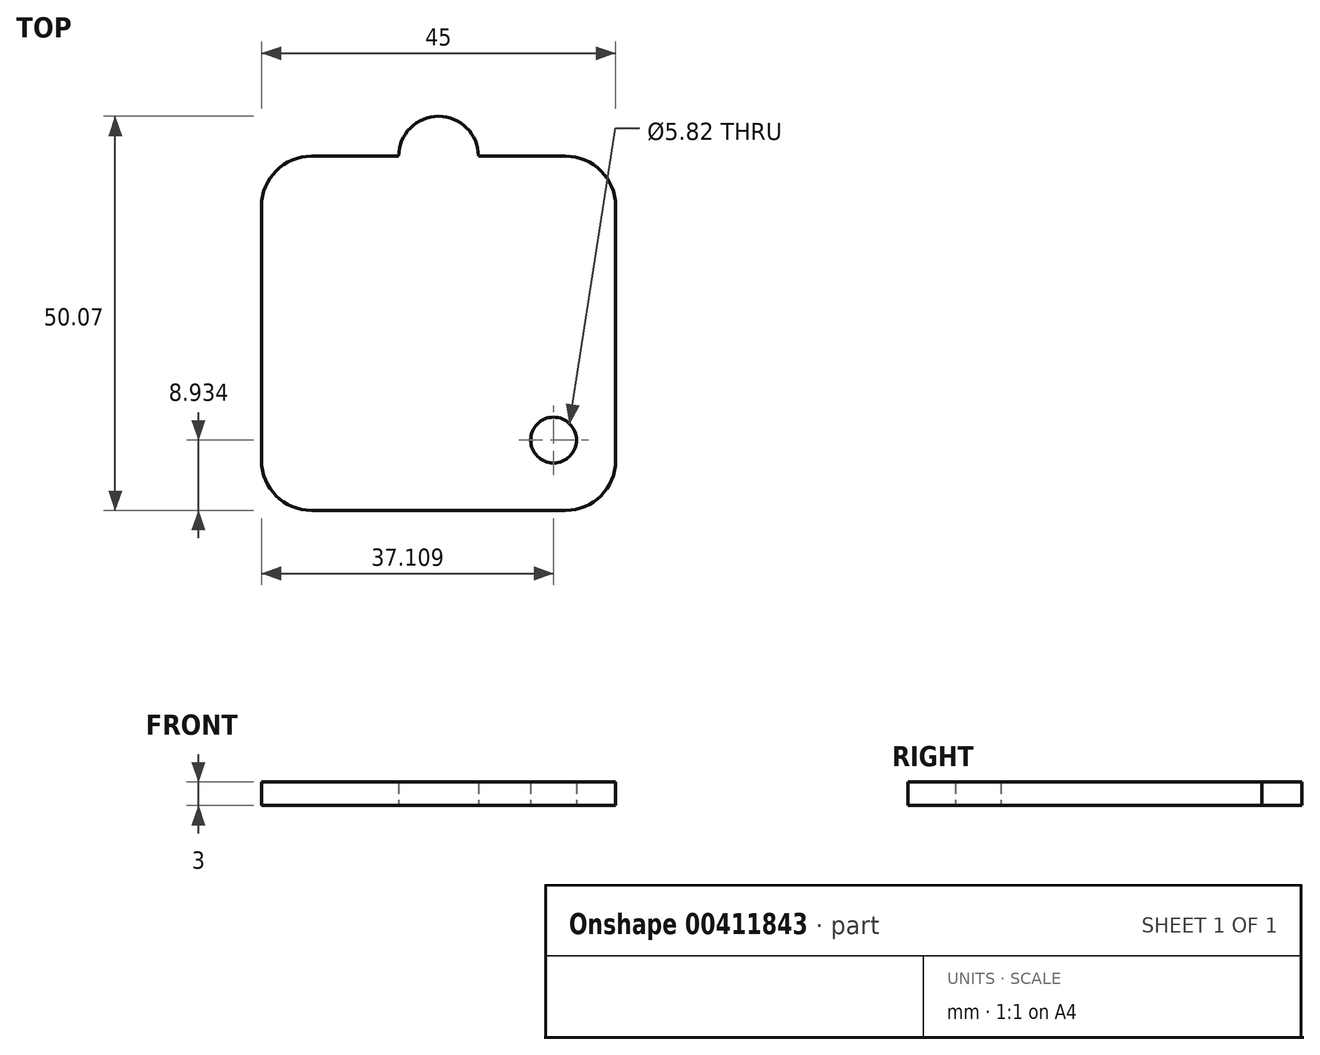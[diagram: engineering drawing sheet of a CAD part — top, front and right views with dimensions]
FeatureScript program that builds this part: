
annotation { "Feature Type Name" : "Feature", "Feature Type Description" : "" }
export const myFeature = defineFeature(function(context is Context, id is Id, definition is map)
    precondition{}
    {
        {
            var Q0;
            Q0=qCreatedBy(makeId("Top.planeOp"),FACE);
            var sketch = newSketch(context, id + "F0", { "sketchPlane" : qUnion([Q0])});
            skLineSegment(sketch, "E0.bottom", {"start": v(16.15, 22.5) * mm, "end": v(-16.15, 22.5) * mm});
            skLineSegment(sketch, "E0.top", {"start": v(16.15, -22.5) * mm, "end": v(-16.15, -22.5) * mm});
            skLineSegment(sketch, "E0.left", {"start": v(22.5, 16.15) * mm, "end": v(22.5, -16.15) * mm});
            skLineSegment(sketch, "E0.right", {"start": v(-22.5, 16.15) * mm, "end": v(-22.5, -16.15) * mm});
            skPoint(sketch, "E0.middle", {"position": v(0, 0) * mm});
            skCircle(sketch, "E1", {"center": v(0, 22.5) * mm, "radius": 5.07 * mm});
            skPoint(sketch, "E2.visualSharp", {"position": v(-22.5, 22.5) * mm});
            skArc(sketch, "E2.filletArc", {"start": v(-16.15, 22.5) * mm, "mid": v(-20.64, 20.64) * mm, "end": v(-22.5, 16.15) * mm});
            skPoint(sketch, "E3.visualSharp", {"position": v(22.5, 22.5) * mm});
            skArc(sketch, "E3.filletArc", {"start": v(22.5, 16.15) * mm, "mid": v(20.64, 20.64) * mm, "end": v(16.15, 22.5) * mm});
            skPoint(sketch, "E4.visualSharp", {"position": v(-22.5, -22.5) * mm});
            skArc(sketch, "E4.filletArc", {"start": v(-22.5, -16.15) * mm, "mid": v(-20.64, -20.64) * mm, "end": v(-16.15, -22.5) * mm});
            skPoint(sketch, "E5.visualSharp", {"position": v(22.5, -22.5) * mm});
            skArc(sketch, "E5.filletArc", {"start": v(16.15, -22.5) * mm, "mid": v(20.64, -20.64) * mm, "end": v(22.5, -16.15) * mm});
            skLineSegment(sketch, "E6.bottom", {"start": v(10, 14.5) * mm, "end": v(-10, 14.5) * mm});
            skLineSegment(sketch, "E6.top", {"start": v(10, -14.5) * mm, "end": v(-10, -14.5) * mm});
            skLineSegment(sketch, "E6.left", {"start": v(10, 14.5) * mm, "end": v(10, -14.5) * mm});
            skLineSegment(sketch, "E6.right", {"start": v(-10, 14.5) * mm, "end": v(-10, -14.5) * mm});
            skPoint(sketch, "E7", {"position": v(-10, 8.5) * mm});
            skPoint(sketch, "E8", {"position": v(-8, 14.5) * mm});
            skCircle(sketch, "E9", {"center": v(-8, 8.5) * mm, "radius": 0.75 * mm});
            skPoint(sketch, "E10", {"position": v(8, -14.5) * mm});
            skPoint(sketch, "E11", {"position": v(10, -8.5) * mm});
            skCircle(sketch, "E12", {"center": v(8, -8.5) * mm, "radius": 0.75 * mm});
            skCircle(sketch, "E13", {"center": v(14.6, -13.57) * mm, "radius": 2.9 * mm});
            skSolve(sketch);
        }
        {
            var Q0;
            Q0=makeQuery(id+"F0.imprint","IMPRINT",FACE,{"disambiguationData":[TD([[makeQuery(id+"F0.imprint","IMPRINT",EDGE,{"derivedFrom":sQuery(id+"F0.wireOp",EDGE,"E9")}),1.0]])]});
            var Q1;
            Q1=makeQuery(id+"F0.imprint","IMPRINT",FACE,{"disambiguationData":[TD([[makeQuery(id+"F0.imprint","IMPRINT",EDGE,{"derivedFrom":sQuery(id+"F0.wireOp",EDGE,"E6.bottom")}),1.0]])]});
            var Q2;
            Q2=makeQuery(id+"F0.imprint","IMPRINT",FACE,{"disambiguationData":[TD([[makeQuery(id+"F0.imprint","IMPRINT",EDGE,{"derivedFrom":sQuery(id+"F0.wireOp",EDGE,"E12")}),1.0]])]});
            var Q3;
            Q3=makeQuery(id+"F0.imprint","IMPRINT",FACE,{"disambiguationData":[TD([[makeQuery(id+"F0.imprint","IMPRINT",EDGE,{"derivedFrom":sQuery(id+"F0.wireOp",EDGE,"E0.top")}),-1.0]])]});
            var Q4;
            {var subQ0=sQuery(id+"F0.wireOp",EDGE,"E1");var subQ1=sQuery(id+"F0.wireOp",EDGE,"E0.bottom");var subQ2=makeQuery(id+"F0.imprint","INTERSECT",VERTEX,{"disambiguationData":[OD(0.0)],"derivedFrom":[subQ1,subQ0]});Q4=makeQuery(id+"F0.imprint","IMPRINT",FACE,{"disambiguationData":[TD([[makeQuery(id+"F0.imprint","IMPRINT",EDGE,{"disambiguationData":[TD([[subQ2,-1.0]])],"derivedFrom":subQ1}),1.0]])]});}
            var Q5;
            {var subQ0=sQuery(id+"F0.wireOp",EDGE,"E1");var subQ1=sQuery(id+"F0.wireOp",EDGE,"E0.bottom");var subQ2=makeQuery(id+"F0.imprint","INTERSECT",VERTEX,{"disambiguationData":[OD(0.0)],"derivedFrom":[subQ1,subQ0]});Q5=makeQuery(id+"F0.imprint","IMPRINT",FACE,{"disambiguationData":[TD([[makeQuery(id+"F0.imprint","IMPRINT",EDGE,{"disambiguationData":[TD([[subQ2,-1.0]])],"derivedFrom":subQ1}),-1.0]])]});}
            extrude(context, id + "F1", {"entities" : qUnion([Q0, Q1, Q2, Q3, Q4, Q5]), "depth" : 3 * mm});
        }
    });
